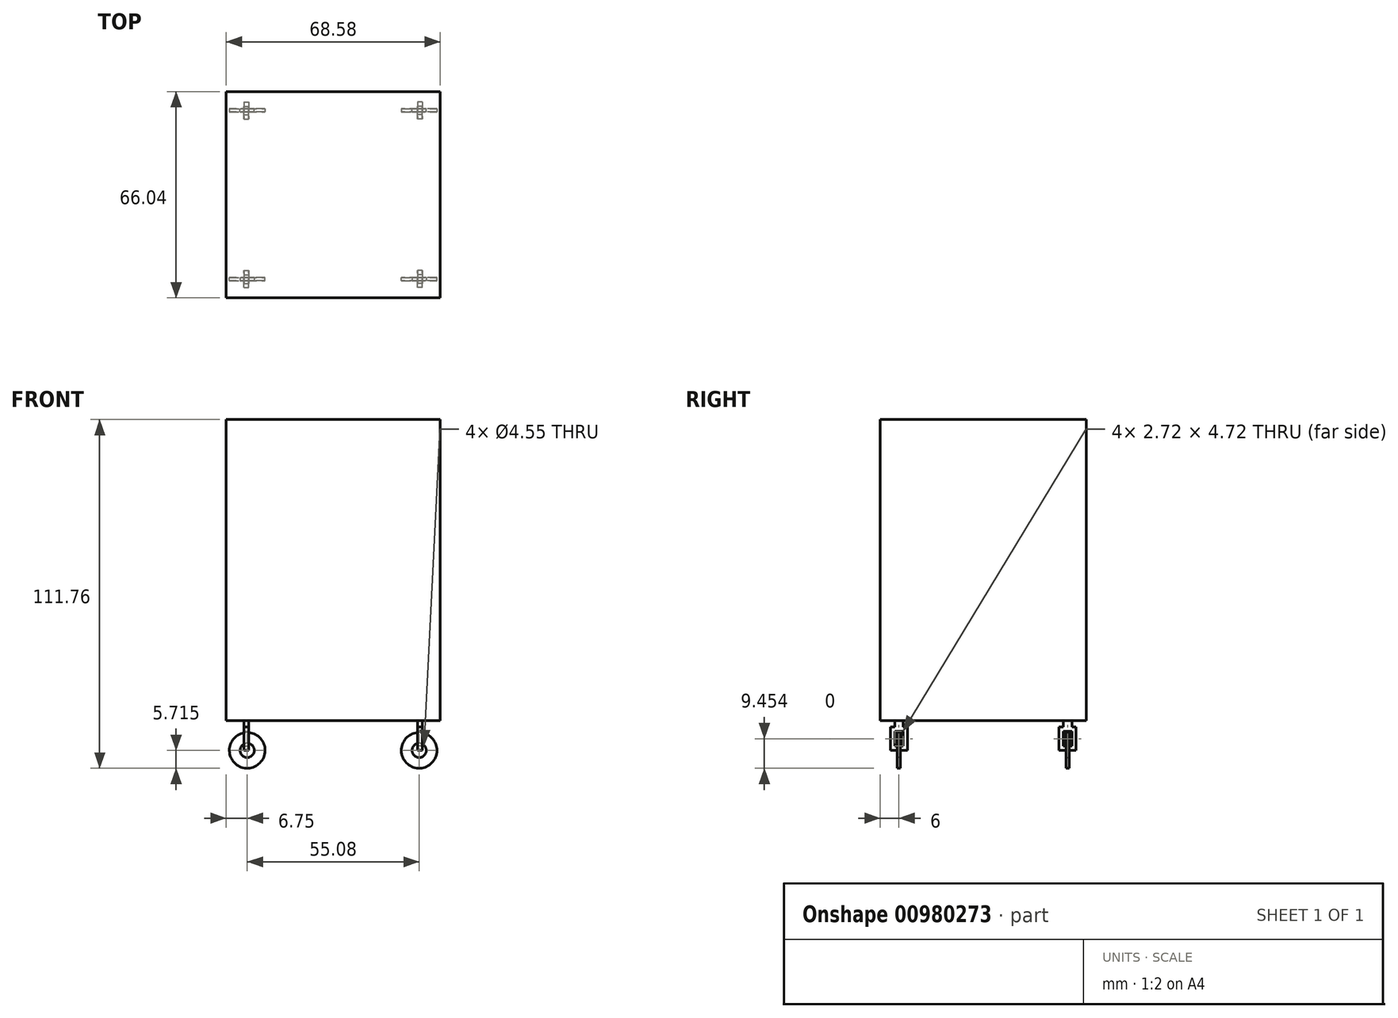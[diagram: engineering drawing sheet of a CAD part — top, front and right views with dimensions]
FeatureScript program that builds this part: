
annotation { "Feature Type Name" : "Feature", "Feature Type Description" : "" }
export const myFeature = defineFeature(function(context is Context, id is Id, definition is map)
    precondition{}
    {
        {
            var Q0;
            Q0=qCreatedBy(makeId("Top.planeOp"),FACE);
            var sketch = newSketch(context, id + "F0", { "sketchPlane" : qUnion([Q0])});
            skLineSegment(sketch, "E0.bottom", {"start": v(-34.29, -33.02) * mm, "end": v(34.3, -33.02) * mm});
            skLineSegment(sketch, "E0.top", {"start": v(-34.29, 33.02) * mm, "end": v(34.29, 33.02) * mm});
            skLineSegment(sketch, "E0.left", {"start": v(-34.29, -33.02) * mm, "end": v(-34.3, 33.02) * mm});
            skLineSegment(sketch, "E0.right", {"start": v(34.3, -33.02) * mm, "end": v(34.3, 33.02) * mm});
            skPoint(sketch, "E0.middle", {"position": v(0, 0) * mm});
            skLineSegment(sketch, "E1.bottom", {"start": v(-34.29, 33.02) * mm, "end": v(-20.79, 33.02) * mm});
            skLineSegment(sketch, "E1.top", {"start": v(-34.29, 20.02) * mm, "end": v(-20.79, 20.02) * mm});
            skLineSegment(sketch, "E1.left", {"start": v(-34.3, 33.02) * mm, "end": v(-34.3, 20.02) * mm});
            skLineSegment(sketch, "E1.right", {"start": v(-20.79, 33.02) * mm, "end": v(-20.79, 20.02) * mm});
            skLineSegment(sketch, "E2.0.1.0", {"start": v(-34.29, -33.02) * mm, "end": v(-20.79, -33.02) * mm});
            skLineSegment(sketch, "E2.0.1.1", {"start": v(-20.79, -20.02) * mm, "end": v(-20.79, -33.02) * mm});
            skLineSegment(sketch, "E2.0.1.2", {"start": v(-34.29, -20.02) * mm, "end": v(-20.79, -20.02) * mm});
            skLineSegment(sketch, "E2.0.1.3", {"start": v(-34.29, -20.02) * mm, "end": v(-34.29, -33.02) * mm});
            skLineSegment(sketch, "E2.1.0.0", {"start": v(20.8, 20.02) * mm, "end": v(34.3, 20.02) * mm});
            skLineSegment(sketch, "E2.1.0.1", {"start": v(34.3, 33.02) * mm, "end": v(34.3, 20.02) * mm});
            skLineSegment(sketch, "E2.1.0.2", {"start": v(20.8, 33.02) * mm, "end": v(34.3, 33.02) * mm});
            skLineSegment(sketch, "E2.1.0.3", {"start": v(20.8, 33.02) * mm, "end": v(20.8, 20.02) * mm});
            skLineSegment(sketch, "E2.1.1.0", {"start": v(20.8, -33.02) * mm, "end": v(34.3, -33.02) * mm});
            skLineSegment(sketch, "E2.1.1.1", {"start": v(34.3, -20.02) * mm, "end": v(34.3, -33.02) * mm});
            skLineSegment(sketch, "E2.1.1.2", {"start": v(20.8, -20.02) * mm, "end": v(34.3, -20.02) * mm});
            skLineSegment(sketch, "E2.1.1.3", {"start": v(20.8, -20.02) * mm, "end": v(20.8, -33.02) * mm});
            skLineSegment(sketch, "E2.direction2", {"start": v(-34.3, 20.02) * mm, "end": v(-34.3, -33.02) * mm, "construction": true});
            skSolve(sketch);
        }
        {
            var Q0;
            {var subQ3=sQuery(id+"F0.wireOp",EDGE,"E1.top");Q0=makeQuery(id+"F0.imprint","IMPRINT",FACE,{"disambiguationData":[TD([[makeQuery(id+"F0.imprint","IMPRINT",EDGE,{"derivedFrom":subQ3}),-1.0]])]});}
            var Q1;
            {var subQ0=sQuery(id+"F0.wireOp",EDGE,"E2.0.1.1");Q1=makeQuery(id+"F0.imprint","IMPRINT",FACE,{"disambiguationData":[TD([[makeQuery(id+"F0.imprint","IMPRINT",EDGE,{"derivedFrom":subQ0}),-1.0]])]});}
            var Q2;
            {var subQ4=sQuery(id+"F0.wireOp",EDGE,"E1.top");Q2=makeQuery(id+"F0.imprint","IMPRINT",FACE,{"disambiguationData":[TD([[makeQuery(id+"F0.imprint","IMPRINT",EDGE,{"derivedFrom":subQ4}),1.0]])]});}
            var Q3;
            {var subQ4=sQuery(id+"F0.wireOp",EDGE,"E2.1.1.2");Q3=makeQuery(id+"F0.imprint","IMPRINT",FACE,{"disambiguationData":[TD([[makeQuery(id+"F0.imprint","IMPRINT",EDGE,{"derivedFrom":subQ4}),-1.0]])]});}
            var Q4;
            {var subQ4=sQuery(id+"F0.wireOp",EDGE,"E2.1.0.0");Q4=makeQuery(id+"F0.imprint","IMPRINT",FACE,{"disambiguationData":[TD([[makeQuery(id+"F0.imprint","IMPRINT",EDGE,{"derivedFrom":subQ4}),1.0]])]});}
            extrude(context, id + "F1", {"entities" : qUnion([Q0, Q1, Q2, Q3, Q4]), "depth" : 111.76 * mm, "offsetDistance" : 25 * mm, "hasSecondDirection" : true, "secondDirectionOppositeDirection" : false, "secondDirectionDepth" : 15.24 * mm});
        }
        {
            var Q0;
            {var subQ3=sQuery(id+"F0.wireOp",EDGE,"E1.top");Q0=makeQuery(id+"F0.imprint","IMPRINT",FACE,{"disambiguationData":[TD([[makeQuery(id+"F0.imprint","IMPRINT",EDGE,{"derivedFrom":subQ3}),-1.0]])]});}
            extrude(context, id + "F2", {"entities" : qUnion([Q0]), "operationType" : NewBodyOperationType.ADD, "depth" : 25 * mm, "offsetDistance" : 25 * mm});
        }
        {
            var Q0;
            Q0=makeQuery(id+"F2.opExtrude","SWEPT_FACE",FACE,{"disambiguationData":[OSD([sQuery(id+"F0.wireOp",EDGE,"E1.top")])]});
            var sketch = newSketch(context, id + "F3", { "sketchPlane" : qUnion([Q0])});
            skCircle(sketch, "E3", {"center": v(27.54, 5.72) * mm, "radius": 5.72 * mm});
            skLineSegment(sketch, "E4", {"start": v(27.54, 0) * mm, "end": v(27.54, 11.43) * mm});
            skSolve(sketch);
        }
        {
            var Q0;
            {var subQ0=sQuery(id+"F3.wireOp",EDGE,"E4");Q0=makeQuery(id+"F3.imprint","IMPRINT",FACE,{"disambiguationData":[TD([[makeQuery(id+"F3.imprint","IMPRINT",EDGE,{"derivedFrom":subQ0}),1.0]])]});}
            var Q1;
            {var subQ0=sQuery(id+"F3.wireOp",EDGE,"E4");Q1=makeQuery(id+"F3.imprint","IMPRINT",FACE,{"disambiguationData":[TD([[makeQuery(id+"F3.imprint","IMPRINT",EDGE,{"derivedFrom":subQ0}),-1.0]])]});}
            extrude(context, id + "F4", {"entities" : qUnion([Q0, Q1]), "depth" : 7.5 * mm, "offsetDistance" : 25 * mm, "hasSecondDirection" : true, "secondDirectionOppositeDirection" : false, "secondDirectionDepth" : 6.5 * mm});
        }
        {
            var Q0;
            Q0=makeQuery(id+"F4.opExtrude","CAP_FACE",FACE,{"disambiguationData":[OSD([sQuery(id+"F3.wireOp",EDGE,"E3")])],"isStart":false});
            var sketch = newSketch(context, id + "F5", { "sketchPlane" : qUnion([Q0])});
            skLineSegment(sketch, "E5", {"start": v(27.54, 0) * mm, "end": v(27.54, 11.43) * mm, "construction": true});
            skCircle(sketch, "E6", {"center": v(27.54, 5.72) * mm, "radius": 2.27 * mm});
            skSolve(sketch);
        }
        {
            var Q0;
            Q0=makeQuery(id+"F5.imprint","IMPRINT",FACE,{"disambiguationData":[TD([[makeQuery(id+"F5.imprint","IMPRINT",EDGE,{"derivedFrom":sQuery(id+"F5.wireOp",EDGE,"E6")}),1.0]])]});
            extrude(context, id + "F6", {"entities" : qUnion([Q0]), "operationType" : NewBodyOperationType.REMOVE, "oppositeDirection" : true, "depth" : 25 * mm, "offsetDistance" : 25 * mm});
        }
        {
            var Q0;
            Q0=makeQuery(id+"F4.opExtrude","SWEPT_BODY",BODY,{"disambiguationData":[OSD([sQuery(id+"F3.wireOp",EDGE,"E3")])]});
            var Q1;
            Q1=qCreatedBy(makeId("Right.planeOp"),FACE);
            mirror(context, id + "F7", {"entities" : qUnion([Q0]), "mirrorPlane" : qUnion([Q1])});
        }
        {
            var Q0;
            Q0=makeQuery(id+"F7.opPattern","COPY",BODY,{"derivedFrom":makeQuery(id+"F4.opExtrude","SWEPT_BODY",BODY,{"disambiguationData":[OSD([sQuery(id+"F3.wireOp",EDGE,"E3")])]}),"instanceName":"1"});
            var Q1;
            Q1=makeQuery(id+"F4.opExtrude","SWEPT_BODY",BODY,{"disambiguationData":[OSD([sQuery(id+"F3.wireOp",EDGE,"E3")])]});
            var Q2;
            Q2=qCreatedBy(makeId("Front.planeOp"),FACE);
            mirror(context, id + "F8", {"entities" : qUnion([Q0, Q1]), "mirrorPlane" : qUnion([Q2])});
        }
        {
            var Q0;
            Q0=makeQuery(id+"F2.opExtrude","SWEPT_FACE",FACE,{"disambiguationData":[OSD([sQuery(id+"F0.wireOp",EDGE,"E1.right")])]});
            var sketch = newSketch(context, id + "F9", { "sketchPlane" : qUnion([Q0])});
            skLineSegment(sketch, "E7", {"start": v(-26.52, 15.24) * mm, "end": v(-27.02, 15.24) * mm, "construction": true});
            skLineSegment(sketch, "E8", {"start": v(-27.02, 15.24) * mm, "end": v(-27.02, 11.82) * mm});
            skLineSegment(sketch, "E9", {"start": v(-27.02, 11.82) * mm, "end": v(-25.66, 11.82) * mm});
            skLineSegment(sketch, "E10", {"start": v(-25.66, 11.82) * mm, "end": v(-25.66, 5.73) * mm});
            skLineSegment(sketch, "E11", {"start": v(-25.66, 5.73) * mm, "end": v(-24.3, 5.73) * mm});
            skLineSegment(sketch, "E12", {"start": v(-27.02, 11.82) * mm, "end": v(-27.02, 13.18) * mm});
            skLineSegment(sketch, "E13", {"start": v(-24.3, 5.73) * mm, "end": v(-24.3, 13.18) * mm});
            skLineSegment(sketch, "E14", {"start": v(-24.3, 13.18) * mm, "end": v(-25.66, 13.18) * mm});
            skLineSegment(sketch, "E15", {"start": v(-25.66, 13.18) * mm, "end": v(-25.66, 15.24) * mm});
            skLineSegment(sketch, "E16.MirrorCS", {"start": v(-27.02, 11.82) * mm, "end": v(-28.38, 11.82) * mm});
            skLineSegment(sketch, "E17.MirrorCS", {"start": v(-28.38, 13.18) * mm, "end": v(-28.38, 15.24) * mm});
            skLineSegment(sketch, "E18.MirrorCS", {"start": v(-29.74, 13.18) * mm, "end": v(-28.38, 13.18) * mm});
            skLineSegment(sketch, "E19.MirrorCS", {"start": v(-29.74, 5.73) * mm, "end": v(-29.74, 13.18) * mm});
            skLineSegment(sketch, "E20.MirrorCS", {"start": v(-28.38, 11.82) * mm, "end": v(-28.38, 5.73) * mm});
            skLineSegment(sketch, "E21.MirrorCS", {"start": v(-28.38, 5.73) * mm, "end": v(-29.74, 5.73) * mm});
            skLineSegment(sketch, "E22", {"start": v(-28.38, 5.73) * mm, "end": v(-28.38, 7.1) * mm});
            skLineSegment(sketch, "E23.bottom", {"start": v(-28.38, 7.1) * mm, "end": v(-25.66, 7.1) * mm});
            skLineSegment(sketch, "E23.top", {"start": v(-28.38, 5.73) * mm, "end": v(-25.66, 5.73) * mm});
            skLineSegment(sketch, "E23.left", {"start": v(-28.38, 7.1) * mm, "end": v(-28.38, 5.73) * mm});
            skLineSegment(sketch, "E23.right", {"start": v(-25.66, 7.1) * mm, "end": v(-25.66, 5.73) * mm});
            skSolve(sketch);
        }
        {
            var Q0;
            {var subQ1=sQuery(id+"F9.wireOp",EDGE,"E9");Q0=makeQuery(id+"F9.imprint","IMPRINT",FACE,{"disambiguationData":[TD([[makeQuery(id+"F9.imprint","IMPRINT",EDGE,{"derivedFrom":subQ1}),1.0]])]});}
            var Q1;
            {var subQ0=sQuery(id+"F9.wireOp",EDGE,"E16.MirrorCS");Q1=makeQuery(id+"F9.imprint","IMPRINT",FACE,{"disambiguationData":[TD([[makeQuery(id+"F9.imprint","IMPRINT",EDGE,{"derivedFrom":subQ0}),-1.0]])]});}
            var Q2;
            {var subQ2=sQuery(id+"F9.wireOp",EDGE,"E23.bottom");Q2=makeQuery(id+"F9.imprint","IMPRINT",FACE,{"disambiguationData":[TD([[makeQuery(id+"F9.imprint","IMPRINT",EDGE,{"derivedFrom":subQ2}),-1.0]])]});}
            extrude(context, id + "F10", {"entities" : qUnion([Q0, Q1, Q2]), "depth" : 7.75 * mm, "offsetDistance" : 25 * mm, "hasSecondDirection" : true, "secondDirectionOppositeDirection" : false, "secondDirectionDepth" : 6.25 * mm});
        }
        {
            var Q0;
            Q0=makeQuery(id+"F10.opExtrude","SWEPT_BODY",BODY,{"disambiguationData":[OSD([sQuery(id+"F0.wireOp",EDGE,"E0.bottom"),sQuery(id+"F0.wireOp",EDGE,"E0.top"),sQuery(id+"F0.wireOp",EDGE,"E0.left"),sQuery(id+"F0.wireOp",EDGE,"E0.right"),sQuery(id+"F0.wireOp",EDGE,"E1.right"),sQuery(id+"F9.wireOp",EDGE,"E9"),sQuery(id+"F9.wireOp",EDGE,"E10"),sQuery(id+"F9.wireOp",EDGE,"E11"),sQuery(id+"F9.wireOp",EDGE,"E13"),sQuery(id+"F9.wireOp",EDGE,"E14"),sQuery(id+"F9.wireOp",EDGE,"E15"),sQuery(id+"F9.wireOp",EDGE,"E16.MirrorCS"),sQuery(id+"F9.wireOp",EDGE,"E17.MirrorCS"),sQuery(id+"F9.wireOp",EDGE,"E18.MirrorCS"),sQuery(id+"F9.wireOp",EDGE,"E19.MirrorCS"),sQuery(id+"F9.wireOp",EDGE,"E20.MirrorCS"),sQuery(id+"F9.wireOp",EDGE,"E21.MirrorCS"),sQuery(id+"F9.wireOp",EDGE,"E23.bottom"),sQuery(id+"F9.wireOp",EDGE,"E23.top")])]});
            var Q1;
            Q1=qCreatedBy(makeId("Front.planeOp"),FACE);
            mirror(context, id + "F11", {"entities" : qUnion([Q0]), "mirrorPlane" : qUnion([Q1])});
        }
        {
            var Q0;
            Q0=makeQuery(id+"F10.opExtrude","SWEPT_BODY",BODY,{"disambiguationData":[OSD([sQuery(id+"F0.wireOp",EDGE,"E0.bottom"),sQuery(id+"F0.wireOp",EDGE,"E0.top"),sQuery(id+"F0.wireOp",EDGE,"E0.left"),sQuery(id+"F0.wireOp",EDGE,"E0.right"),sQuery(id+"F0.wireOp",EDGE,"E1.right"),sQuery(id+"F9.wireOp",EDGE,"E9"),sQuery(id+"F9.wireOp",EDGE,"E10"),sQuery(id+"F9.wireOp",EDGE,"E11"),sQuery(id+"F9.wireOp",EDGE,"E13"),sQuery(id+"F9.wireOp",EDGE,"E14"),sQuery(id+"F9.wireOp",EDGE,"E15"),sQuery(id+"F9.wireOp",EDGE,"E16.MirrorCS"),sQuery(id+"F9.wireOp",EDGE,"E17.MirrorCS"),sQuery(id+"F9.wireOp",EDGE,"E18.MirrorCS"),sQuery(id+"F9.wireOp",EDGE,"E19.MirrorCS"),sQuery(id+"F9.wireOp",EDGE,"E20.MirrorCS"),sQuery(id+"F9.wireOp",EDGE,"E21.MirrorCS"),sQuery(id+"F9.wireOp",EDGE,"E23.bottom"),sQuery(id+"F9.wireOp",EDGE,"E23.top")])]});
            var Q1;
            Q1=makeQuery(id+"F11.opPattern","COPY",BODY,{"derivedFrom":makeQuery(id+"F10.opExtrude","SWEPT_BODY",BODY,{"disambiguationData":[OSD([sQuery(id+"F0.wireOp",EDGE,"E0.bottom"),sQuery(id+"F0.wireOp",EDGE,"E0.top"),sQuery(id+"F0.wireOp",EDGE,"E0.left"),sQuery(id+"F0.wireOp",EDGE,"E0.right"),sQuery(id+"F0.wireOp",EDGE,"E1.right"),sQuery(id+"F9.wireOp",EDGE,"E9"),sQuery(id+"F9.wireOp",EDGE,"E10"),sQuery(id+"F9.wireOp",EDGE,"E11"),sQuery(id+"F9.wireOp",EDGE,"E13"),sQuery(id+"F9.wireOp",EDGE,"E14"),sQuery(id+"F9.wireOp",EDGE,"E15"),sQuery(id+"F9.wireOp",EDGE,"E16.MirrorCS"),sQuery(id+"F9.wireOp",EDGE,"E17.MirrorCS"),sQuery(id+"F9.wireOp",EDGE,"E18.MirrorCS"),sQuery(id+"F9.wireOp",EDGE,"E19.MirrorCS"),sQuery(id+"F9.wireOp",EDGE,"E20.MirrorCS"),sQuery(id+"F9.wireOp",EDGE,"E21.MirrorCS"),sQuery(id+"F9.wireOp",EDGE,"E23.bottom"),sQuery(id+"F9.wireOp",EDGE,"E23.top")])]}),"instanceName":"1"});
            var Q2;
            Q2=qCreatedBy(makeId("Right.planeOp"),FACE);
            mirror(context, id + "F12", {"operationType" : NewBodyOperationType.ADD, "entities" : qUnion([Q0, Q1]), "mirrorPlane" : qUnion([Q2])});
        }
        {
            var Q0;
            {var subQ0=sQuery(id+"F0.wireOp",EDGE,"E0.bottom");Q0=makeQuery(id+"F2.boolean.opBoolean","MERGE",FACE,{"derivedFrom":[makeQuery(id+"F1.opExtrude","SWEPT_FACE",FACE,{"disambiguationData":[OSD([subQ0])]}),makeQuery(id+"F2.opExtrude","SWEPT_FACE",FACE,{"disambiguationData":[OSD([subQ0])]})]});}
            var sketch = newSketch(context, id + "F13", { "sketchPlane" : qUnion([Q0])});
            skLineSegment(sketch, "E24.bottom", {"start": v(-20.79, 15.24) * mm, "end": v(20.8, 15.24) * mm});
            skLineSegment(sketch, "E24.top", {"start": v(-20.79, 0) * mm, "end": v(20.8, 0) * mm});
            skLineSegment(sketch, "E24.left", {"start": v(-20.79, 15.24) * mm, "end": v(-20.79, 0) * mm});
            skLineSegment(sketch, "E24.right", {"start": v(20.8, 15.24) * mm, "end": v(20.8, 0) * mm});
            skSolve(sketch);
        }
        {
            var Q0;
            Q0=makeQuery(id+"F13.imprint","IMPRINT",FACE,{"disambiguationData":[TD([[makeQuery(id+"F13.imprint","IMPRINT",EDGE,{"derivedFrom":sQuery(id+"F13.wireOp",EDGE,"E24.bottom")}),-1.0]])]});
            extrude(context, id + "F14", {"entities" : qUnion([Q0]), "operationType" : NewBodyOperationType.REMOVE, "oppositeDirection" : true, "depth" : 100 * mm, "offsetDistance" : 25 * mm});
        }
        {
            var Q0;
            {var subQ0=sQuery(id+"F0.wireOp",EDGE,"E0.right");Q0=makeQuery(id+"F2.boolean.opBoolean","MERGE",FACE,{"derivedFrom":[makeQuery(id+"F1.opExtrude","SWEPT_FACE",FACE,{"disambiguationData":[OSD([subQ0])]}),makeQuery(id+"F2.opExtrude","SWEPT_FACE",FACE,{"disambiguationData":[OSD([subQ0])]})]});}
            var sketch = newSketch(context, id + "F15", { "sketchPlane" : qUnion([Q0])});
            skLineSegment(sketch, "E25.bottom", {"start": v(-20.02, 15.24) * mm, "end": v(20.02, 15.24) * mm});
            skLineSegment(sketch, "E25.top", {"start": v(-20.02, 0) * mm, "end": v(20.02, 0) * mm});
            skLineSegment(sketch, "E25.left", {"start": v(-20.02, 15.24) * mm, "end": v(-20.02, 0) * mm});
            skLineSegment(sketch, "E25.right", {"start": v(20.02, 15.24) * mm, "end": v(20.02, 0) * mm});
            skSolve(sketch);
        }
        {
            var Q0;
            Q0 = qSketchRegion(id + "F15", true);
            extrude(context, id + "F16", {"entities" : qUnion([Q0]), "operationType" : NewBodyOperationType.REMOVE, "oppositeDirection" : true, "depth" : 100 * mm, "offsetDistance" : 25 * mm});
        }
    });
